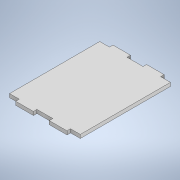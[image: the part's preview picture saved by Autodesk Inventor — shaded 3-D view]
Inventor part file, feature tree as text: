
AUTODESK INVENTOR PART (.ipt)
format: ipt  version: 2022 (Build 260153000, 153)  size: 124,416 bytes
history: native  units: mm
features: sheet_metal_op x1, sketch x1, other x1
ambient origin geometry x8: Origin, YZ Plane, XZ Plane, XY Plane, X Axis, Y Axis, Z Axis, Center Point
bodies: Solid1 (feature_tree)
feature tree (3):
  sheet_metal_op  "Face1"
  sketch  "Sketch1"  dims[d1=40.0mm d2=10.0mm d3=10.0mm d4=5.5mm d5=5.5mm d6=2.0mm d7=25.5mm d8=2.0mm]
  other  "Plate1"
